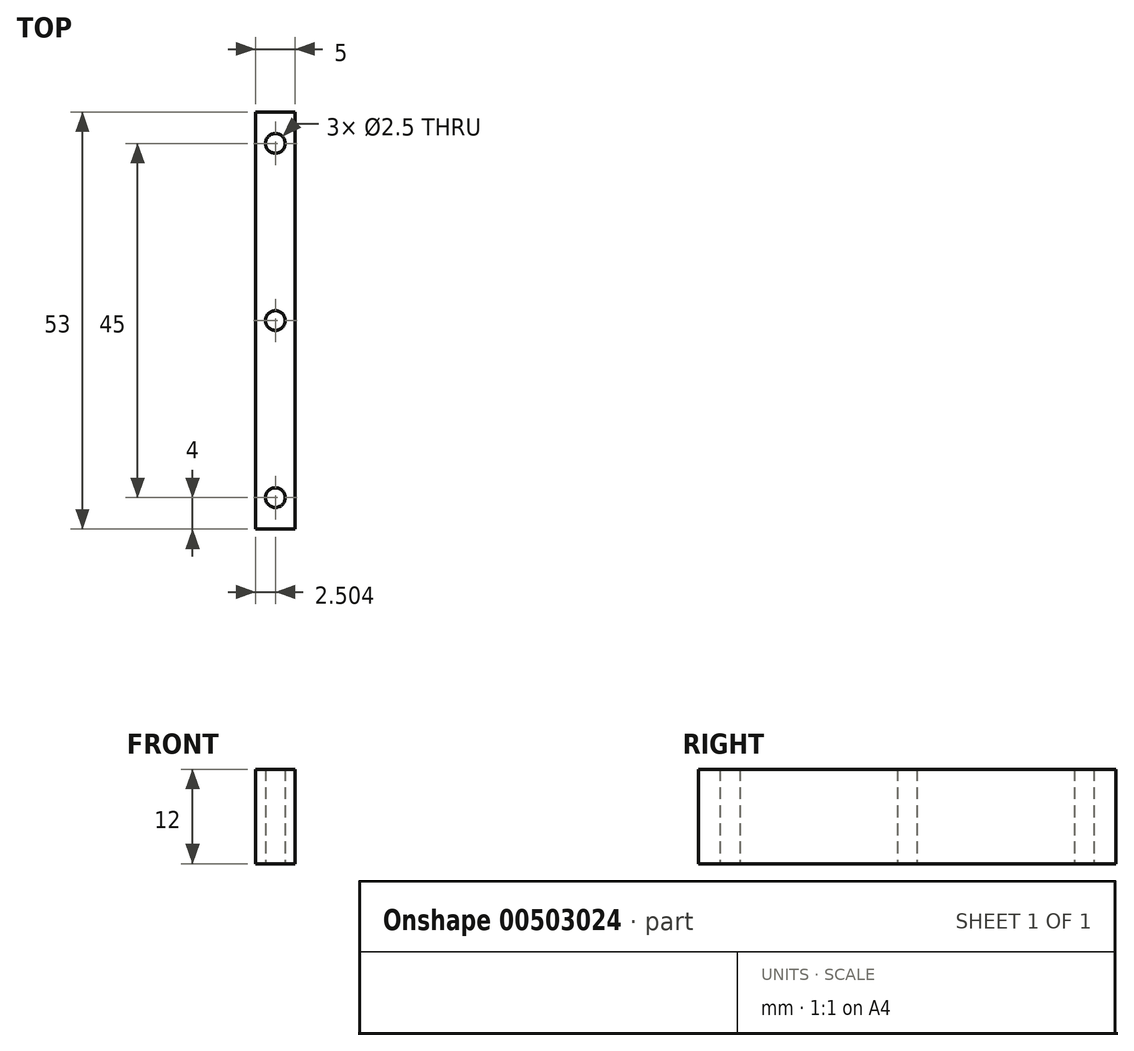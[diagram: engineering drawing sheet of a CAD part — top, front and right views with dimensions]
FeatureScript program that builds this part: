
annotation { "Feature Type Name" : "Feature", "Feature Type Description" : "" }
export const myFeature = defineFeature(function(context is Context, id is Id, definition is map)
    precondition{}
    {
        {
            var Q0;
            Q0=qCreatedBy(makeId("Top.planeOp"),FACE);
            var sketch = newSketch(context, id + "F0", { "sketchPlane" : qUnion([Q0])});
            skLineSegment(sketch, "E0.bottom", {"start": v(-6.35, 26.5) * mm, "end": v(-1.35, 26.5) * mm});
            skLineSegment(sketch, "E0.top", {"start": v(-6.35, -26.5) * mm, "end": v(-1.35, -26.5) * mm});
            skLineSegment(sketch, "E0.left", {"start": v(-6.35, 26.5) * mm, "end": v(-6.35, -26.5) * mm});
            skLineSegment(sketch, "E0.right", {"start": v(-1.35, 26.5) * mm, "end": v(-1.35, -26.5) * mm});
            skCircle(sketch, "E1", {"center": v(-3.85, 22.5) * mm, "radius": 1.25 * mm});
            skCircle(sketch, "E2", {"center": v(-3.85, 0) * mm, "radius": 1.25 * mm});
            skCircle(sketch, "E3", {"center": v(-3.85, -22.5) * mm, "radius": 1.25 * mm});
            skLineSegment(sketch, "E4", {"start": v(-3.85, 26.5) * mm, "end": v(-3.85, -26.5) * mm, "construction": true});
            skLineSegment(sketch, "E5", {"start": v(-3.85, 22.5) * mm, "end": v(-3.85, 22.5) * mm});
            skSolve(sketch);
        }
        {
            var Q0;
            Q0=makeQuery(id+"F0.imprint","IMPRINT",FACE,{"disambiguationData":[TD([[makeQuery(id+"F0.imprint","IMPRINT",EDGE,{"derivedFrom":sQuery(id+"F0.wireOp",EDGE,"E0.bottom")}),-1.0]])]});
            extrude(context, id + "F1", {"entities" : qUnion([Q0]), "depth" : 12 * mm});
        }
    });
